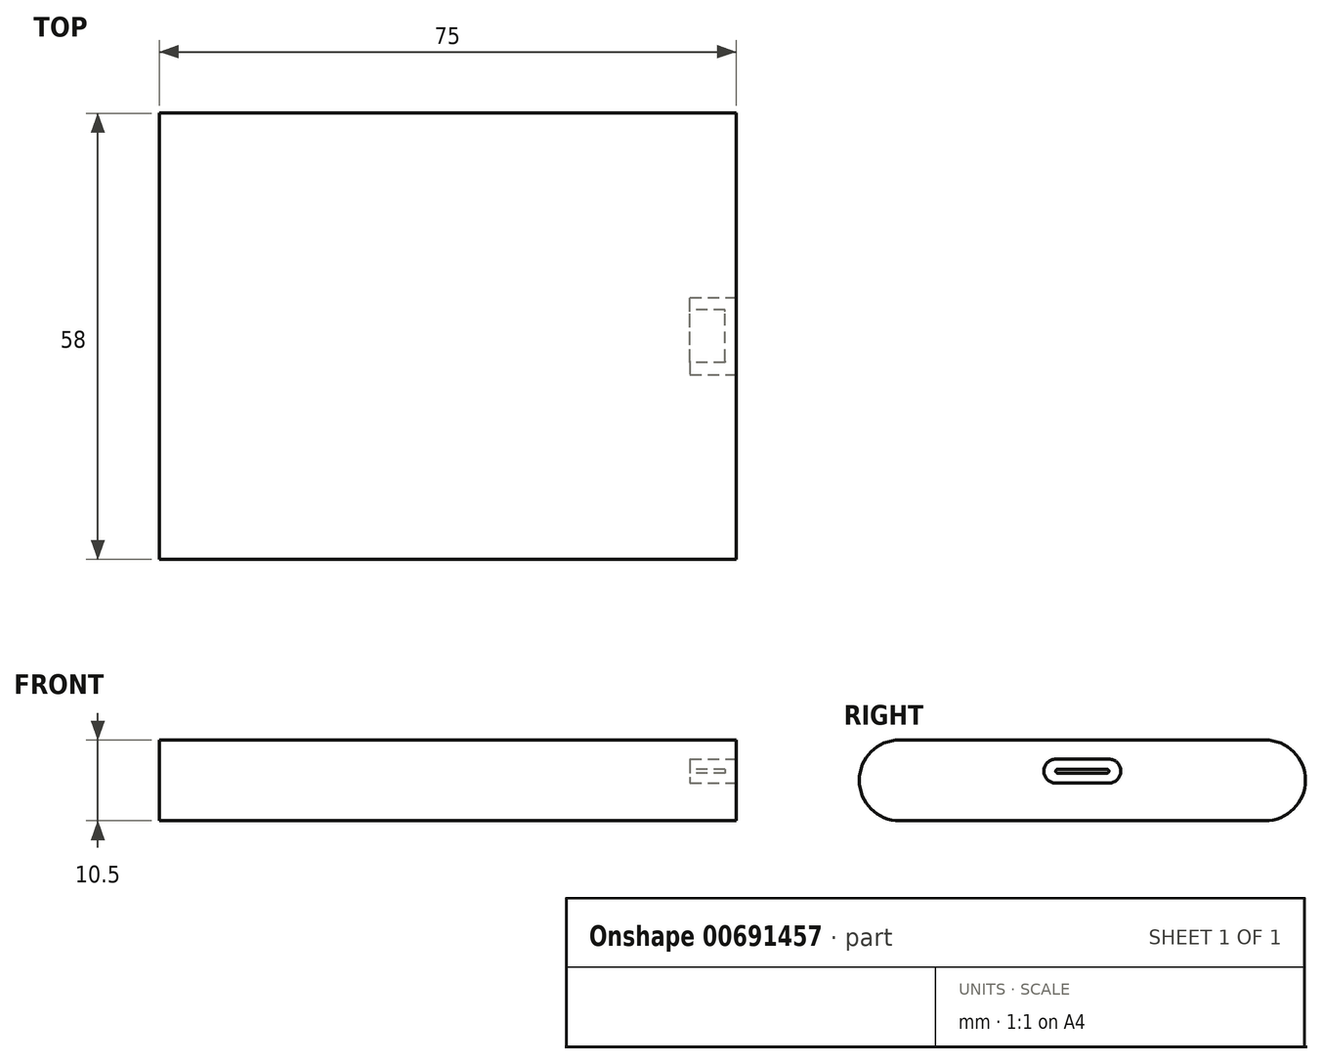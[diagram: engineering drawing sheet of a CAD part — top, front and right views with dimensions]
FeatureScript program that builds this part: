
annotation { "Feature Type Name" : "Feature", "Feature Type Description" : "" }
export const myFeature = defineFeature(function(context is Context, id is Id, definition is map)
    precondition{}
    {
        {
            var Q0;
            Q0=qCreatedBy(makeId("Top.planeOp"),FACE);
            var sketch = newSketch(context, id + "F0", { "sketchPlane" : qUnion([Q0])});
            skLineSegment(sketch, "E0.bottom", {"start": v(-55.45, -42.5) * mm, "end": v(19.55, -42.5) * mm});
            skLineSegment(sketch, "E0.top", {"start": v(-55.45, 15.5) * mm, "end": v(19.55, 15.5) * mm});
            skLineSegment(sketch, "E0.left", {"start": v(-55.45, -42.5) * mm, "end": v(-55.45, 15.5) * mm});
            skLineSegment(sketch, "E0.right", {"start": v(19.55, -42.5) * mm, "end": v(19.55, 15.5) * mm});
            skSolve(sketch);
        }
        {
            var Q0;
            Q0=makeQuery(id+"F0.imprint","IMPRINT",FACE,{"disambiguationData":[TD([[makeQuery(id+"F0.imprint","IMPRINT",EDGE,{"derivedFrom":sQuery(id+"F0.wireOp",EDGE,"E0.bottom")}),1.0]])]});
            extrude(context, id + "F1", {"entities" : qUnion([Q0]), "depth" : 10.5 * mm, "offsetDistance" : 25.4 * mm});
        }
        {
            var Q0;
            Q0=makeQuery(id+"F1.opExtrude","SWEPT_FACE",FACE,{"disambiguationData":[OSD([sQuery(id+"F0.wireOp",EDGE,"E0.right")])]});
            var sketch = newSketch(context, id + "F2", { "sketchPlane" : qUnion([Q0])});
            skLineSegment(sketch, "E1", {"start": v(-13.5, 8) * mm, "end": v(-18.5, 8) * mm});
            skLineSegment(sketch, "E2", {"start": v(-13.5, 8) * mm, "end": v(-8.5, 8) * mm});
            skLineSegment(sketch, "E3", {"start": v(-8.5, 8) * mm, "end": v(-8.5, 4.9) * mm});
            skLineSegment(sketch, "E4", {"start": v(-8.5, 4.9) * mm, "end": v(-18.5, 4.9) * mm});
            skLineSegment(sketch, "E5", {"start": v(-18.5, 4.9) * mm, "end": v(-18.5, 8) * mm});
            skCircle(sketch, "E6", {"center": v(-16.95, 6.45) * mm, "radius": 1.55 * mm});
            skCircle(sketch, "E7", {"center": v(-10.05, 6.45) * mm, "radius": 1.55 * mm});
            skLineSegment(sketch, "E8", {"start": v(-16.95, 8) * mm, "end": v(-16.95, 4.9) * mm});
            skLineSegment(sketch, "E9", {"start": v(-10.05, 8) * mm, "end": v(-10.05, 4.9) * mm});
            skSolve(sketch);
        }
        {
            var Q0;
            Q0=makeQuery(id+"F1.opExtrude","CAP_EDGE",EDGE,{"disambiguationData":[OSD([sQuery(id+"F0.wireOp",EDGE,"E0.bottom")])],"isStart":false});
            var Q1;
            Q1=makeQuery(id+"F1.opExtrude","CAP_EDGE",EDGE,{"disambiguationData":[OSD([sQuery(id+"F0.wireOp",EDGE,"E0.bottom")])],"isStart":true});
            var Q2;
            Q2=makeQuery(id+"F1.opExtrude","CAP_EDGE",EDGE,{"disambiguationData":[OSD([sQuery(id+"F0.wireOp",EDGE,"E0.top")])],"isStart":false});
            var Q3;
            Q3=makeQuery(id+"F1.opExtrude","CAP_EDGE",EDGE,{"disambiguationData":[OSD([sQuery(id+"F0.wireOp",EDGE,"E0.top")])],"isStart":true});
            fillet(context, id + "F3", {"entities" : qUnion([Q0, Q1, Q2, Q3]), "radius" : 5.25 * mm, "tangentPropagation" : true, "allowEdgeOverflow" : false});
        }
        {
            var Q0;
            {var subQ2=sQuery(id+"F2.wireOp",EDGE,"E1");var subQ6=sQuery(id+"F2.wireOp",EDGE,"E2");var subQ7=makeQuery(id+"F2.imprint","INTERSECT",VERTEX,{"derivedFrom":[subQ2,subQ6]});Q0=makeQuery(id+"F2.imprint","IMPRINT",FACE,{"disambiguationData":[TD([[makeQuery(id+"F2.imprint","IMPRINT",EDGE,{"disambiguationData":[TD([[subQ7,-1.0]])],"derivedFrom":subQ2}),1.0]])]});}
            var Q1;
            {var subQ0=sQuery(id+"F2.wireOp",EDGE,"E9");Q1=makeQuery(id+"F2.imprint","IMPRINT",FACE,{"disambiguationData":[TD([[makeQuery(id+"F2.imprint","IMPRINT",EDGE,{"derivedFrom":subQ0}),-1.0]])]});}
            var Q2;
            {var subQ0=sQuery(id+"F2.wireOp",EDGE,"E9");Q2=makeQuery(id+"F2.imprint","IMPRINT",FACE,{"disambiguationData":[TD([[makeQuery(id+"F2.imprint","IMPRINT",EDGE,{"derivedFrom":subQ0}),1.0]])]});}
            var Q3;
            {var subQ0=sQuery(id+"F2.wireOp",EDGE,"E8");Q3=makeQuery(id+"F2.imprint","IMPRINT",FACE,{"disambiguationData":[TD([[makeQuery(id+"F2.imprint","IMPRINT",EDGE,{"derivedFrom":subQ0}),1.0]])]});}
            var Q4;
            {var subQ0=sQuery(id+"F2.wireOp",EDGE,"E8");Q4=makeQuery(id+"F2.imprint","IMPRINT",FACE,{"disambiguationData":[TD([[makeQuery(id+"F2.imprint","IMPRINT",EDGE,{"derivedFrom":subQ0}),-1.0]])]});}
            extrude(context, id + "F4", {"entities" : qUnion([Q0, Q1, Q2, Q3, Q4]), "operationType" : NewBodyOperationType.REMOVE, "oppositeDirection" : true, "depth" : 6 * mm, "offsetDistance" : 25.4 * mm});
        }
        {
            var Q0;
            Q0=makeQuery(id+"F4.boolean.opBoolean","COPY",FACE,{"derivedFrom":makeQuery(id+"F4.opExtrude","CAP_FACE",FACE,{"disambiguationData":[OSD([sQuery(id+"F2.wireOp",EDGE,"E1"),sQuery(id+"F2.wireOp",EDGE,"E2"),sQuery(id+"F2.wireOp",EDGE,"E4"),sQuery(id+"F2.wireOp",EDGE,"E6"),sQuery(id+"F2.wireOp",EDGE,"E7")])],"isStart":false})});
            var sketch = newSketch(context, id + "F5", { "sketchPlane" : qUnion([Q0])});
            skLineSegment(sketch, "E10", {"start": v(-16.95, 8) * mm, "end": v(-16.95, 4.9) * mm});
            skLineSegment(sketch, "E11", {"start": v(-10.05, 8) * mm, "end": v(-10.05, 4.9) * mm});
            skLineSegment(sketch, "E12", {"start": v(-16.95, 6.45) * mm, "end": v(-10.05, 6.45) * mm});
            skLineSegment(sketch, "E13.top", {"start": v(-16.95, 6.7) * mm, "end": v(-10.05, 6.7) * mm});
            skLineSegment(sketch, "E13.left", {"start": v(-16.95, 6.45) * mm, "end": v(-16.95, 6.7) * mm});
            skLineSegment(sketch, "E13.right", {"start": v(-10.05, 6.45) * mm, "end": v(-10.05, 6.7) * mm});
            skLineSegment(sketch, "E14.left", {"start": v(-16.95, 6.45) * mm, "end": v(-16.95, 6.2) * mm});
            skLineSegment(sketch, "E14.right", {"start": v(-10.05, 6.45) * mm, "end": v(-10.05, 6.2) * mm});
            skLineSegment(sketch, "E15.top", {"start": v(-16.95, 6.2) * mm, "end": v(-10.05, 6.2) * mm});
            skSolve(sketch);
        }
        {
            var Q0;
            Q0=makeQuery(id+"F5.imprint","IMPRINT",FACE,{"disambiguationData":[TD([[makeQuery(id+"F5.imprint","IMPRINT",EDGE,{"derivedFrom":sQuery(id+"F5.wireOp",EDGE,"E13.top")}),-1.0]])]});
            var Q1;
            Q1=makeQuery(id+"F5.imprint","IMPRINT",FACE,{"disambiguationData":[TD([[makeQuery(id+"F5.imprint","IMPRINT",EDGE,{"derivedFrom":sQuery(id+"F5.wireOp",EDGE,"E12")}),-1.0]])]});
            extrude(context, id + "F6", {"entities" : qUnion([Q0, Q1]), "operationType" : NewBodyOperationType.ADD, "depth" : 4.57 * mm, "offsetDistance" : 25.4 * mm});
        }
        {
            var Q0;
            Q0=makeQuery(id+"F6.opExtrude","SWEPT_EDGE",EDGE,{"disambiguationData":[OSD([sQuery(id+"F5.wireOp",EDGE,"E11"),sQuery(id+"F5.wireOp",EDGE,"E13.top"),sQuery(id+"F5.wireOp",EDGE,"E13.right")])]});
            var Q1;
            Q1=makeQuery(id+"F6.opExtrude","SWEPT_EDGE",EDGE,{"disambiguationData":[OSD([sQuery(id+"F5.wireOp",EDGE,"E14.right"),sQuery(id+"F5.wireOp",EDGE,"E15.top"),sQuery(id+"F5.wireOp",EDGE,"E14.right")])]});
            var Q2;
            Q2=makeQuery(id+"F6.opExtrude","SWEPT_EDGE",EDGE,{"disambiguationData":[OSD([sQuery(id+"F5.wireOp",EDGE,"E10"),sQuery(id+"F5.wireOp",EDGE,"E13.top"),sQuery(id+"F5.wireOp",EDGE,"E13.left")])]});
            var Q3;
            Q3=makeQuery(id+"F6.opExtrude","SWEPT_EDGE",EDGE,{"disambiguationData":[OSD([sQuery(id+"F5.wireOp",EDGE,"E14.left"),sQuery(id+"F5.wireOp",EDGE,"E15.top"),sQuery(id+"F5.wireOp",EDGE,"E14.left")])]});
            fillet(context, id + "F7", {"entities" : qUnion([Q0, Q1, Q2, Q3]), "radius" : .25 * mm, "tangentPropagation" : true, "allowEdgeOverflow" : false});
        }
    });
